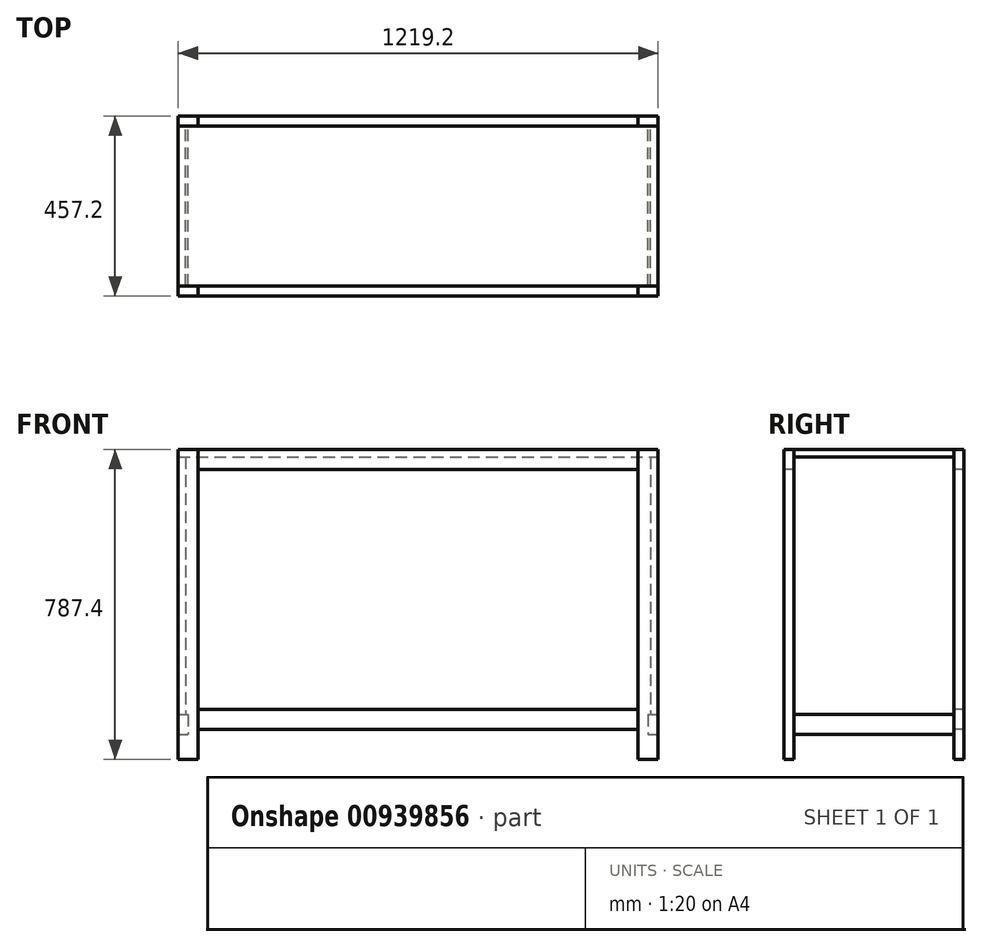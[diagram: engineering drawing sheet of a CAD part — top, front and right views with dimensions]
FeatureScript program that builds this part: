
annotation { "Feature Type Name" : "Feature", "Feature Type Description" : "" }
export const myFeature = defineFeature(function(context is Context, id is Id, definition is map)
    precondition{}
    {
        {
            var Q0;
            Q0=qCreatedBy(makeId("Front.planeOp"),FACE);
            var sketch = newSketch(context, id + "F0", { "sketchPlane" : qUnion([Q0])});
            skLineSegment(sketch, "E0", {"start": v(-1219.2, 0) * mm, "end": v(0, 0) * mm, "construction": true});
            skLineSegment(sketch, "E1", {"start": v(0, 787.4) * mm, "end": v(-1219.2, 787.4) * mm, "construction": true});
            skLineSegment(sketch, "E2", {"start": v(-1219.2, 787.4) * mm, "end": v(-1219.2, 121.35) * mm, "construction": true});
            skLineSegment(sketch, "E3", {"start": v(0, 787.4) * mm, "end": v(0, 102.3) * mm, "construction": true});
            skLineSegment(sketch, "E4.0", {"start": v(-19.05, 768.35) * mm, "end": v(-19.05, 102.3) * mm, "construction": true});
            skLineSegment(sketch, "E5.0", {"start": v(-1200.15, 768.35) * mm, "end": v(-1200.15, 121.35) * mm, "construction": true});
            skLineSegment(sketch, "E6.0", {"start": v(0, 768.35) * mm, "end": v(-1219.2, 768.35) * mm, "construction": true});
            skLineSegment(sketch, "E7.trimOffspring", {"start": v(-1200.15, 121.35) * mm, "end": v(-1219.2, 121.35) * mm, "construction": true});
            skLineSegment(sketch, "E8.bottom", {"start": v(-1219.2, 787.4) * mm, "end": v(0, 787.4) * mm});
            skLineSegment(sketch, "E8.top", {"start": v(-1219.2, 768.35) * mm, "end": v(0, 768.35) * mm});
            skLineSegment(sketch, "E8.left", {"start": v(-1219.2, 787.4) * mm, "end": v(-1219.2, 768.35) * mm});
            skLineSegment(sketch, "E8.right", {"start": v(0, 787.4) * mm, "end": v(0, 768.35) * mm});
            skLineSegment(sketch, "E9.bottom", {"start": v(-1219.2, 768.35) * mm, "end": v(-1200.15, 768.35) * mm});
            skLineSegment(sketch, "E9.left", {"start": v(-1219.2, 768.35) * mm, "end": v(-1219.2, 121.35) * mm});
            skLineSegment(sketch, "E9.right", {"start": v(-1200.15, 768.35) * mm, "end": v(-1200.15, 121.35) * mm});
            skLineSegment(sketch, "E10.bottom", {"start": v(-19.05, 768.35) * mm, "end": v(0, 768.35) * mm});
            skLineSegment(sketch, "E10.left", {"start": v(-19.05, 768.35) * mm, "end": v(-19.05, 121.35) * mm});
            skLineSegment(sketch, "E10.right", {"start": v(0, 768.35) * mm, "end": v(0, 102.3) * mm});
            skLineSegment(sketch, "E11.right", {"start": v(-19.05, 121.35) * mm, "end": v(-19.05, 102.3) * mm});
            skLineSegment(sketch, "E12.bottom", {"start": v(-1200.15, 121.35) * mm, "end": v(-1219.2, 121.35) * mm});
            skLineSegment(sketch, "E12.top", {"start": v(-1200.15, 768.35) * mm, "end": v(-1219.2, 768.35) * mm});
            skLineSegment(sketch, "E12.left", {"start": v(-1200.15, 121.35) * mm, "end": v(-1200.15, 768.35) * mm});
            skLineSegment(sketch, "E12.right", {"start": v(-1219.2, 121.35) * mm, "end": v(-1219.2, 768.35) * mm});
            skLineSegment(sketch, "E13.bottom", {"start": v(-19.05, 102.3) * mm, "end": v(0, 102.3) * mm});
            skLineSegment(sketch, "E13.left", {"start": v(-19.05, 102.3) * mm, "end": v(-19.05, 768.35) * mm});
            skLineSegment(sketch, "E13.right", {"start": v(0, 102.3) * mm, "end": v(0, 768.35) * mm});
            skLineSegment(sketch, "E14.bottom", {"start": v(-1219.2, 121.35) * mm, "end": v(-1200.15, 121.35) * mm});
            skLineSegment(sketch, "E15.trimOffspring", {"start": v(-1219.2, 70.55) * mm, "end": v(-1219.2, 0) * mm, "construction": true});
            skLineSegment(sketch, "E16.trimOffspring", {"start": v(0, 88.9) * mm, "end": v(0, 0) * mm, "construction": true});
            skSolve(sketch);
        }
        {
            var Q0;
            Q0=makeQuery(id+"F0.imprint","IMPRINT",FACE,{"disambiguationData":[TD([[makeQuery(id+"F0.imprint","IMPRINT",EDGE,{"derivedFrom":sQuery(id+"F0.wireOp",EDGE,"E8.bottom")}),-1.0]])]});
            extrude(context, id + "F1", {"entities" : qUnion([Q0]), "depth" : 406.4 * mm, "offsetDistance" : 25.4 * mm});
        }
        {
            var Q0;
            Q0=makeQuery(id+"F1.opExtrude","SWEPT_FACE",FACE,{"disambiguationData":[OSD([sQuery(id+"F0.wireOp",EDGE,"E8.bottom")])]});
            var sketch = newSketch(context, id + "F2", { "sketchPlane" : qUnion([Q0])});
            skLineSegment(sketch, "E17.0", {"start": v(-1219.2, -431.8) * mm, "end": v(0, -431.8) * mm});
            skLineSegment(sketch, "E18.bottom", {"start": v(-50.8, -406.4) * mm, "end": v(0, -406.4) * mm});
            skLineSegment(sketch, "E18.top", {"start": v(-50.8, -431.8) * mm, "end": v(0, -431.8) * mm});
            skLineSegment(sketch, "E18.left", {"start": v(-50.8, -406.4) * mm, "end": v(-50.8, -431.8) * mm});
            skLineSegment(sketch, "E18.right", {"start": v(0, -406.4) * mm, "end": v(0, -431.8) * mm});
            skLineSegment(sketch, "E19.bottom", {"start": v(-1168.4, -406.4) * mm, "end": v(-1219.2, -406.4) * mm});
            skLineSegment(sketch, "E19.top", {"start": v(-1168.4, -431.8) * mm, "end": v(-1219.2, -431.8) * mm});
            skLineSegment(sketch, "E19.left", {"start": v(-1168.4, -406.4) * mm, "end": v(-1168.4, -431.8) * mm});
            skLineSegment(sketch, "E19.right", {"start": v(-1219.2, -406.4) * mm, "end": v(-1219.2, -431.8) * mm});
            skLineSegment(sketch, "E20.0", {"start": v(-1193.8, -406.4) * mm, "end": v(-1193.8, 0) * mm});
            skLineSegment(sketch, "E21.0", {"start": v(-25.4, -406.4) * mm, "end": v(-25.4, 0) * mm});
            skLineSegment(sketch, "E22.bottom", {"start": v(-1219.2, 0) * mm, "end": v(-1193.8, 0) * mm});
            skLineSegment(sketch, "E22.top", {"start": v(-1219.2, -406.4) * mm, "end": v(-1193.8, -406.4) * mm});
            skLineSegment(sketch, "E22.left", {"start": v(-1219.2, 0) * mm, "end": v(-1219.2, -406.4) * mm});
            skLineSegment(sketch, "E22.right", {"start": v(-1193.8, 0) * mm, "end": v(-1193.8, -406.4) * mm});
            skSolve(sketch);
        }
        {
            var Q0;
            {var subQ0=sQuery(id+"F2.wireOp",EDGE,"E19.left");Q0=makeQuery(id+"F2.imprint","IMPRINT",FACE,{"disambiguationData":[TD([[makeQuery(id+"F2.imprint","IMPRINT",EDGE,{"derivedFrom":subQ0}),-1.0]])]});}
            extrude(context, id + "F3", {"entities" : qUnion([Q0]), "oppositeDirection" : true, "depth" : 787.4 * mm, "offsetDistance" : 25.4 * mm});
        }
        {
            var Q0;
            {var subQ0=sQuery(id+"F2.wireOp",EDGE,"E18.left");Q0=makeQuery(id+"F2.imprint","IMPRINT",FACE,{"disambiguationData":[TD([[makeQuery(id+"F2.imprint","IMPRINT",EDGE,{"derivedFrom":subQ0}),1.0]])]});}
            extrude(context, id + "F4", {"entities" : qUnion([Q0]), "oppositeDirection" : true, "depth" : 787.4 * mm, "offsetDistance" : 25.4 * mm});
        }
        {
            var Q0;
            {var subQ2=sQuery(id+"F2.wireOp",EDGE,"E18.left");Q0=makeQuery(id+"F2.imprint","IMPRINT",FACE,{"disambiguationData":[TD([[makeQuery(id+"F2.imprint","IMPRINT",EDGE,{"derivedFrom":subQ2}),-1.0]])]});}
            extrude(context, id + "F5", {"entities" : qUnion([Q0]), "oppositeDirection" : true, "depth" : 50.8 * mm, "offsetDistance" : 25.4 * mm});
        }
        {
            var Q0;
            Q0=makeQuery(id+"F5.opExtrude","SWEPT_BODY",BODY,{"disambiguationData":[OSD([sQuery(id+"F0.wireOp",EDGE,"E8.bottom"),sQuery(id+"F2.wireOp",EDGE,"E17.0"),sQuery(id+"F2.wireOp",EDGE,"E18.left"),sQuery(id+"F2.wireOp",EDGE,"E19.left")])]});
            transform(context, id + "F6", {"entities" : qUnion([Q0]), "transformType" : TransformType.COPY});
        }
        {
            var Q0;
            Q0=makeQuery(id+"F5.opExtrude","SWEPT_BODY",BODY,{"disambiguationData":[OSD([sQuery(id+"F0.wireOp",EDGE,"E8.bottom"),sQuery(id+"F2.wireOp",EDGE,"E17.0"),sQuery(id+"F2.wireOp",EDGE,"E18.left"),sQuery(id+"F2.wireOp",EDGE,"E19.left")])]});
            transform(context, id + "F7", {"entities" : qUnion([Q0]), "transformType" : TransformType.TRANSLATION_3D, "dx" : 0 * mm, "dy" : 0 * mm, "dz" : -330.2 * mm, "makeCopy" : false});
        }
        {
            var Q0;
            Q0=makeQuery(id+"F5.opExtrude","SWEPT_BODY",BODY,{"disambiguationData":[OSD([sQuery(id+"F0.wireOp",EDGE,"E8.bottom"),sQuery(id+"F2.wireOp",EDGE,"E17.0"),sQuery(id+"F2.wireOp",EDGE,"E18.left"),sQuery(id+"F2.wireOp",EDGE,"E19.left")])]});
            transform(context, id + "F8", {"entities" : qUnion([Q0]), "transformType" : TransformType.TRANSLATION_3D, "dx" : 0 * mm, "dy" : 0 * mm, "dz" : -330.2 * mm, "makeCopy" : false});
        }
        {
            var Q0;
            Q0=makeQuery(id+"F3.opExtrude","SWEPT_BODY",BODY,{"disambiguationData":[OSD([sQuery(id+"F2.wireOp",EDGE,"E17.0"),sQuery(id+"F2.wireOp",EDGE,"E19.bottom"),sQuery(id+"F2.wireOp",EDGE,"E19.left"),sQuery(id+"F2.wireOp",EDGE,"E19.right")])]});
            var Q1;
            Q1=makeQuery(id+"F6.opPattern","COPY",BODY,{"derivedFrom":makeQuery(id+"F5.opExtrude","SWEPT_BODY",BODY,{"disambiguationData":[OSD([sQuery(id+"F0.wireOp",EDGE,"E8.bottom"),sQuery(id+"F2.wireOp",EDGE,"E17.0"),sQuery(id+"F2.wireOp",EDGE,"E18.left"),sQuery(id+"F2.wireOp",EDGE,"E19.left")])]}),"instanceName":"1"});
            var Q2;
            Q2=makeQuery(id+"F0Di4ssETCvZlC6_8.opPattern","COPY",BODY,{"derivedFrom":makeQuery(id+"F5.opExtrude","SWEPT_BODY",BODY,{"disambiguationData":[OSD([sQuery(id+"F0.wireOp",EDGE,"E8.bottom"),sQuery(id+"F2.wireOp",EDGE,"E17.0"),sQuery(id+"F2.wireOp",EDGE,"E18.left"),sQuery(id+"F2.wireOp",EDGE,"E19.left")])]}),"instanceName":"1"});
            var Q3;
            Q3=makeQuery(id+"F5.opExtrude","SWEPT_BODY",BODY,{"disambiguationData":[OSD([sQuery(id+"F0.wireOp",EDGE,"E8.bottom"),sQuery(id+"F2.wireOp",EDGE,"E17.0"),sQuery(id+"F2.wireOp",EDGE,"E18.left"),sQuery(id+"F2.wireOp",EDGE,"E19.left")])]});
            var Q4;
            Q4=makeQuery(id+"F4.opExtrude","SWEPT_BODY",BODY,{"disambiguationData":[OSD([sQuery(id+"F2.wireOp",EDGE,"E17.0"),sQuery(id+"F2.wireOp",EDGE,"E18.bottom"),sQuery(id+"F2.wireOp",EDGE,"E18.left"),sQuery(id+"F2.wireOp",EDGE,"E18.right")])]});
            transform(context, id + "F9", {"entities" : qUnion([Q0, Q1, Q2, Q3, Q4]), "transformType" : TransformType.COPY});
        }
        {
            var Q0;
            Q0=makeQuery(id+"F9.opPattern","COPY",BODY,{"derivedFrom":makeQuery(id+"F4.opExtrude","SWEPT_BODY",BODY,{"disambiguationData":[OSD([sQuery(id+"F2.wireOp",EDGE,"E17.0"),sQuery(id+"F2.wireOp",EDGE,"E18.bottom"),sQuery(id+"F2.wireOp",EDGE,"E18.left"),sQuery(id+"F2.wireOp",EDGE,"E18.right")])]}),"instanceName":"1"});
            var Q1;
            Q1=makeQuery(id+"F9.opPattern","COPY",BODY,{"derivedFrom":makeQuery(id+"F5.opExtrude","SWEPT_BODY",BODY,{"disambiguationData":[OSD([sQuery(id+"F0.wireOp",EDGE,"E8.bottom"),sQuery(id+"F2.wireOp",EDGE,"E17.0"),sQuery(id+"F2.wireOp",EDGE,"E18.left"),sQuery(id+"F2.wireOp",EDGE,"E19.left")])]}),"instanceName":"1"});
            var Q2;
            Q2=makeQuery(id+"F9.opPattern","COPY",BODY,{"derivedFrom":makeQuery(id+"F6.opPattern","COPY",BODY,{"derivedFrom":makeQuery(id+"F5.opExtrude","SWEPT_BODY",BODY,{"disambiguationData":[OSD([sQuery(id+"F0.wireOp",EDGE,"E8.bottom"),sQuery(id+"F2.wireOp",EDGE,"E17.0"),sQuery(id+"F2.wireOp",EDGE,"E18.left"),sQuery(id+"F2.wireOp",EDGE,"E19.left")])]}),"instanceName":"1"}),"instanceName":"1"});
            var Q3;
            Q3=makeQuery(id+"F9.opPattern","COPY",BODY,{"derivedFrom":makeQuery(id+"F0Di4ssETCvZlC6_8.opPattern","COPY",BODY,{"derivedFrom":makeQuery(id+"F5.opExtrude","SWEPT_BODY",BODY,{"disambiguationData":[OSD([sQuery(id+"F0.wireOp",EDGE,"E8.bottom"),sQuery(id+"F2.wireOp",EDGE,"E17.0"),sQuery(id+"F2.wireOp",EDGE,"E18.left"),sQuery(id+"F2.wireOp",EDGE,"E19.left")])]}),"instanceName":"1"}),"instanceName":"1"});
            var Q4;
            Q4=makeQuery(id+"F9.opPattern","COPY",BODY,{"derivedFrom":makeQuery(id+"F3.opExtrude","SWEPT_BODY",BODY,{"disambiguationData":[OSD([sQuery(id+"F2.wireOp",EDGE,"E17.0"),sQuery(id+"F2.wireOp",EDGE,"E19.bottom"),sQuery(id+"F2.wireOp",EDGE,"E19.left"),sQuery(id+"F2.wireOp",EDGE,"E19.right")])]}),"instanceName":"1"});
            transform(context, id + "F10", {"entities" : qUnion([Q0, Q1, Q2, Q3, Q4]), "transformType" : TransformType.TRANSLATION_3D, "dx" : 0 * mm, "dy" : 431.8 * mm, "dz" : 0 * mm, "makeCopy" : false});
        }
        {
            var Q0;
            Q0=makeQuery(id+"F5.opExtrude","SWEPT_BODY",BODY,{"disambiguationData":[OSD([sQuery(id+"F0.wireOp",EDGE,"E8.bottom"),sQuery(id+"F2.wireOp",EDGE,"E17.0"),sQuery(id+"F2.wireOp",EDGE,"E18.left"),sQuery(id+"F2.wireOp",EDGE,"E19.left")])]});
            deleteBodies(context, id + "F11", {"entities" : qUnion([Q0])});
        }
        {
            var Q0;
            {var subQ2=sQuery(id+"F2.wireOp",EDGE,"E20.0");Q0=makeQuery(id+"F2.imprint","IMPRINT",FACE,{"disambiguationData":[TD([[makeQuery(id+"F2.imprint","IMPRINT",EDGE,{"derivedFrom":subQ2}),1.0]])]});}
            extrude(context, id + "F12", {"entities" : qUnion([Q0]), "depth" : 50.8 * mm, "offsetDistance" : 25.4 * mm});
        }
        {
            var Q0;
            Q0=makeQuery(id+"F12.opExtrude","SWEPT_BODY",BODY,{"disambiguationData":[OSD([sQuery(id+"F2.wireOp",EDGE,"E19.bottom"),sQuery(id+"F2.wireOp",EDGE,"E20.0"),sQuery(id+"F2.wireOp",EDGE,"E22.bottom"),sQuery(id+"F2.wireOp",EDGE,"E22.left")])]});
            transform(context, id + "F13", {"entities" : qUnion([Q0]), "transformType" : TransformType.TRANSLATION_3D, "dx" : 0 * mm, "dy" : 0 * mm, "dz" : -723.9 * mm, "makeCopy" : false});
        }
        {
            var Q0;
            Q0=makeQuery(id+"F12.opExtrude","SWEPT_BODY",BODY,{"disambiguationData":[OSD([sQuery(id+"F2.wireOp",EDGE,"E19.bottom"),sQuery(id+"F2.wireOp",EDGE,"E20.0"),sQuery(id+"F2.wireOp",EDGE,"E22.bottom"),sQuery(id+"F2.wireOp",EDGE,"E22.left")])]});
            transform(context, id + "F14", {"entities" : qUnion([Q0]), "transformType" : TransformType.COPY});
        }
        {
            var Q0;
            Q0=makeQuery(id+"F14.opPattern","COPY",BODY,{"derivedFrom":makeQuery(id+"F12.opExtrude","SWEPT_BODY",BODY,{"disambiguationData":[OSD([sQuery(id+"F2.wireOp",EDGE,"E19.bottom"),sQuery(id+"F2.wireOp",EDGE,"E20.0"),sQuery(id+"F2.wireOp",EDGE,"E22.bottom"),sQuery(id+"F2.wireOp",EDGE,"E22.left")])]}),"instanceName":"1"});
            transform(context, id + "F15", {"entities" : qUnion([Q0]), "transformType" : TransformType.TRANSLATION_3D, "dx" : 1193.8 * mm, "dy" : 0 * mm, "dz" : 0 * mm, "makeCopy" : false});
        }
        {
            var Q0;
            Q0=makeQuery(id+"F1.opExtrude","SWEPT_FACE",FACE,{"disambiguationData":[OSD([sQuery(id+"F0.wireOp",EDGE,"E8.right")])]});
            var sketch = newSketch(context, id + "F16", { "sketchPlane" : qUnion([Q0])});
            skLineSegment(sketch, "E23.bottom", {"start": v(-406.4, 768.35) * mm, "end": v(0, 768.35) * mm});
            skLineSegment(sketch, "E23.top", {"start": v(-406.4, 114.3) * mm, "end": v(0, 114.3) * mm});
            skLineSegment(sketch, "E23.left", {"start": v(-406.4, 768.35) * mm, "end": v(-406.4, 114.3) * mm});
            skLineSegment(sketch, "E23.right", {"start": v(0, 768.35) * mm, "end": v(0, 114.3) * mm});
            skSolve(sketch);
        }
        {
            var Q0;
            Q0=makeQuery(id+"F16.imprint","IMPRINT",FACE,{"disambiguationData":[TD([[makeQuery(id+"F16.imprint","IMPRINT",EDGE,{"derivedFrom":sQuery(id+"F16.wireOp",EDGE,"E23.bottom")}),-1.0]])]});
            extrude(context, id + "F17", {"entities" : qUnion([Q0]), "oppositeDirection" : true, "depth" : 19.05 * mm, "offsetDistance" : 25.4 * mm});
        }
        {
            var Q0;
            Q0=makeQuery(id+"F17.opExtrude","SWEPT_BODY",BODY,{"disambiguationData":[OSD([sQuery(id+"F16.wireOp",EDGE,"E23.bottom"),sQuery(id+"F16.wireOp",EDGE,"E23.top"),sQuery(id+"F16.wireOp",EDGE,"E23.left"),sQuery(id+"F16.wireOp",EDGE,"E23.right")])]});
            transform(context, id + "F18", {"entities" : qUnion([Q0]), "transformType" : TransformType.COPY});
        }
        {
            var Q0;
            Q0=makeQuery(id+"F18.opPattern","COPY",BODY,{"derivedFrom":makeQuery(id+"F17.opExtrude","SWEPT_BODY",BODY,{"disambiguationData":[OSD([sQuery(id+"F16.wireOp",EDGE,"E23.bottom"),sQuery(id+"F16.wireOp",EDGE,"E23.top"),sQuery(id+"F16.wireOp",EDGE,"E23.left"),sQuery(id+"F16.wireOp",EDGE,"E23.right")])]}),"instanceName":"1"});
            transform(context, id + "F19", {"entities" : qUnion([Q0]), "transformType" : TransformType.TRANSLATION_3D, "dx" : -1200.15 * mm, "dy" : 0 * mm, "dz" : 0 * mm, "makeCopy" : false});
        }
    });
